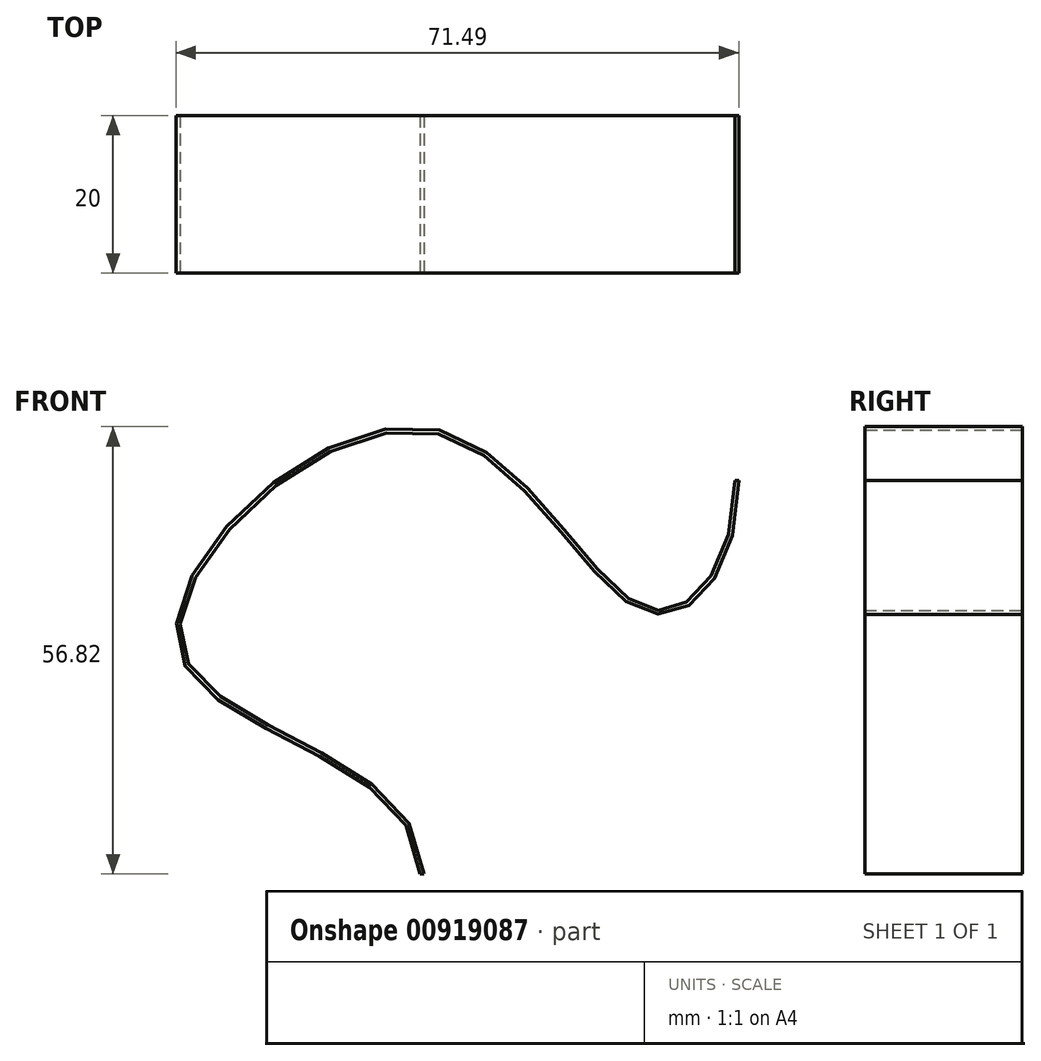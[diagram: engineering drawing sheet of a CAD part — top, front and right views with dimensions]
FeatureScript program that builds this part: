
annotation { "Feature Type Name" : "Feature", "Feature Type Description" : "" }
export const myFeature = defineFeature(function(context is Context, id is Id, definition is map)
    precondition{}
    {
        {
            var Q0;
            Q0=qCreatedBy(makeId("Top.planeOp"),FACE);
            var sketch = newSketch(context, id + "F0", { "sketchPlane" : qUnion([Q0])});
            skLineSegment(sketch, "E0.bottom", {"start": v(0.25, 10) * mm, "end": v(-0.25, 10) * mm});
            skLineSegment(sketch, "E0.top", {"start": v(0.25, -10) * mm, "end": v(-0.25, -10) * mm});
            skLineSegment(sketch, "E0.left", {"start": v(0.25, 10) * mm, "end": v(0.25, -10) * mm});
            skLineSegment(sketch, "E0.right", {"start": v(-0.25, 10) * mm, "end": v(-0.25, -10) * mm});
            skPoint(sketch, "E0.middle", {"position": v(0, 0) * mm});
            skSolve(sketch);
        }
        {
            var Q0;
            Q0=qCreatedBy(makeId("Front.planeOp"),FACE);
            var sketch = newSketch(context, id + "F1", { "sketchPlane" : qUnion([Q0])});
            skFitSpline(sketch, "E1", {"points": [v(0, 0) * mm, v(-30.59, 28.12) * mm, v(0, 56.5) * mm, v(28.45, 33.55) * mm, v(40, 50) * mm], "startDerivative": vector(0, 164.76) * mm, "endDerivative": vector(0, 176.07) * mm});
            skLineSegment(sketch, "E2", {"start": v(0, 0) * mm, "end": v(0, 28.5) * mm, "construction": true});
            skLineSegment(sketch, "E3", {"start": v(40, 50) * mm, "end": v(40, 109.6) * mm, "construction": true});
            skSolve(sketch);
        }
        {
            var Q0;
            Q0=makeQuery(id+"F0.imprint","IMPRINT",FACE,{"disambiguationData":[TD([[makeQuery(id+"F0.imprint","IMPRINT",EDGE,{"derivedFrom":sQuery(id+"F0.wireOp",EDGE,"E0.bottom")}),1.0]])]});
            var Q1;
            Q1=sQuery(id+"F1.wireOp",EDGE,"E1");
            sweep(context, id + "F2", {"profiles" : qUnion([Q0]), "path" : qUnion([Q1])});
        }
    });
